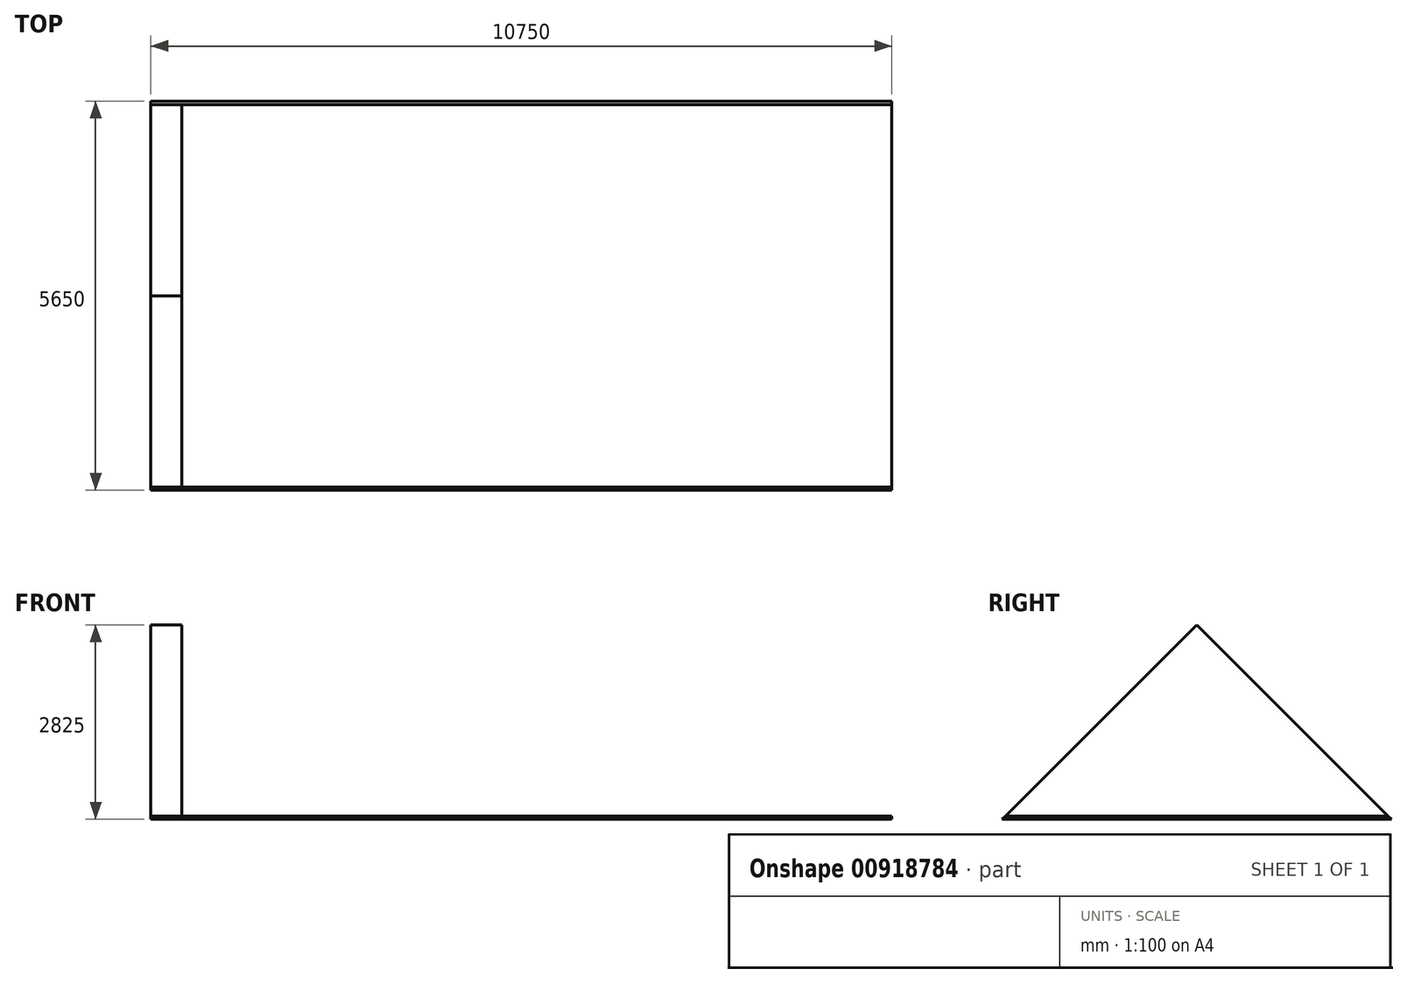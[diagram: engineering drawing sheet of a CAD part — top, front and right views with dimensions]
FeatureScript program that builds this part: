
annotation { "Feature Type Name" : "Feature", "Feature Type Description" : "" }
export const myFeature = defineFeature(function(context is Context, id is Id, definition is map)
    precondition{}
    {
        {
            var Q0;
            Q0=qCreatedBy(makeId("Right.planeOp"),FACE);
            var sketch = newSketch(context, id + "F0", { "sketchPlane" : qUnion([Q0])});
            skLineSegment(sketch, "E0", {"start": v(0, 0) * mm, "end": v(5650, 0) * mm});
            skLineSegment(sketch, "E1", {"start": v(5650, 0) * mm, "end": v(5600, 50) * mm});
            skLineSegment(sketch, "E2", {"start": v(5600, 50) * mm, "end": v(50, 50) * mm});
            skLineSegment(sketch, "E3", {"start": v(50, 50) * mm, "end": v(0, 0) * mm});
            skLineSegment(sketch, "E4", {"start": v(50, 50) * mm, "end": v(2825, 2825) * mm});
            skLineSegment(sketch, "E5", {"start": v(2825, 2825) * mm, "end": v(5600, 50) * mm});
            skLineSegment(sketch, "E6", {"start": v(2825, 2075) * mm, "end": v(3950, 950) * mm});
            skLineSegment(sketch, "E7", {"start": v(3950, 950) * mm, "end": v(1700, 950) * mm});
            skLineSegment(sketch, "E8", {"start": v(1700, 950) * mm, "end": v(2825, 2075) * mm});
            skSolve(sketch);
        }
        {
            var Q0;
            Q0=makeQuery(id+"F0.imprint","IMPRINT",FACE,{"disambiguationData":[TD([[makeQuery(id+"F0.imprint","IMPRINT",EDGE,{"derivedFrom":sQuery(id+"F0.wireOp",EDGE,"E0")}),1.0]])]});
            extrude(context, id + "F1", {"entities" : qUnion([Q0]), "depth" : 10750 * mm, "offsetDistance" : 25 * mm});
        }
        {
            var Q0;
            Q0=makeQuery(id+"F0.imprint","IMPRINT",FACE,{"disambiguationData":[TD([[makeQuery(id+"F0.imprint","IMPRINT",EDGE,{"derivedFrom":sQuery(id+"F0.wireOp",EDGE,"E2")}),-1.0]])]});
            var Q1;
            Q1=makeQuery(id+"F0.imprint","IMPRINT",FACE,{"disambiguationData":[TD([[makeQuery(id+"F0.imprint","IMPRINT",EDGE,{"derivedFrom":sQuery(id+"F0.wireOp",EDGE,"E6")}),-1.0]])]});
            extrude(context, id + "F2", {"entities" : qUnion([Q0, Q1]), "depth" : 450 * mm, "offsetDistance" : 25 * mm});
        }
        {
            var Q0;
            Q0=makeQuery(id+"F0.imprint","IMPRINT",FACE,{"disambiguationData":[TD([[makeQuery(id+"F0.imprint","IMPRINT",EDGE,{"derivedFrom":sQuery(id+"F0.wireOp",EDGE,"E2")}),-1.0]])]});
            var Q1;
            Q1=makeQuery(id+"F0.imprint","IMPRINT",FACE,{"disambiguationData":[TD([[makeQuery(id+"F0.imprint","IMPRINT",EDGE,{"derivedFrom":sQuery(id+"F0.wireOp",EDGE,"E6")}),-1.0]])]});
            extrude(context, id + "F3", {"entities" : qUnion([Q0, Q1]), "depth" : 450 * mm, "offsetDistance" : 25 * mm});
        }
    });
